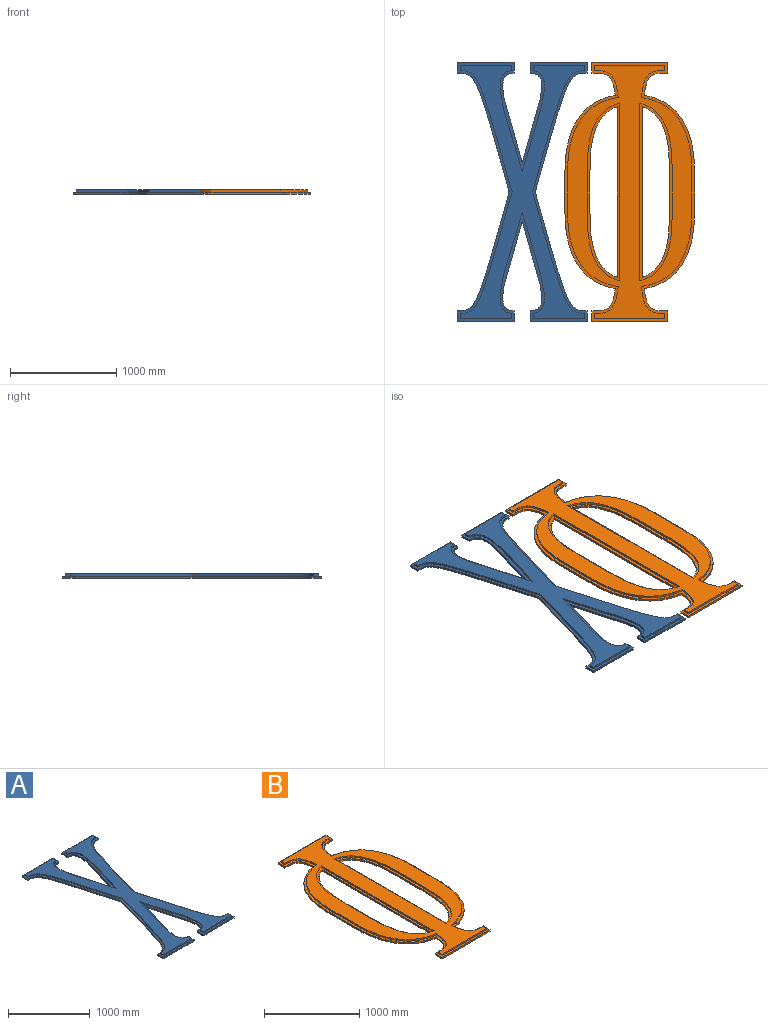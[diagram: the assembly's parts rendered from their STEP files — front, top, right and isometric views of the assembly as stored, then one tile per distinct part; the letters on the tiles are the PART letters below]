
ASSEMBLY  parts=2 mates=2
PART A: 55 faces, bbox 1219.2x2438.4x38.1 mm
  f0: plane 2438.4x1219.2mm, normal (0,0,1), area 313882.5mm2, adj f1,f2,f4,f5,f6,f7,f8,f9
  f1: plane 533.4x19.05mm, normal (0,1,0), area 10161.3mm2, adj f0,f2,f3,f6
  f2: plane 101.6x19.05mm, normal (-1,0,0), area 1935.5mm2, adj f0,f1,f3,f7
  f3: plane 2438.4x1219.2mm, normal (0,0,-1), area 1136315.4mm2, adj f1,f2,f4,f5,f6,f7,f16,f17
  f4: plane 613.66x172.59mm, normal (0.96,0.27,0), area 12143.9mm2, adj f0,f3,f5,f18
  f5: extruded ~224.54x106.77mm, area 5550.7mm2, adj f0,f3,f4,f6
  f6: plane 101.6x19.05mm, normal (1,0,0), area 1935.5mm2, adj f0,f1,f3,f5
  f7: extruded ~1117.6x487.68mm, area 24421.9mm2, adj f0,f2,f3,f34
  f8: plane 50.95x19.05mm, normal (-1,0,0), area 970.5mm2, adj f0,f9,f14,f15
  f9: extruded ~1117.45x481.52mm, area 24198.9mm2, adj f0,f8,f10,f15
  f10: plane 25.4x19.05mm, normal (-0.96,-0.27,0), area 502.7mm2, adj f0,f9,f15,f37
  f11: plane 81.62x25.4mm, normal (0.95,0.3,0), area 1628.3mm2, adj f0,f12,f15,f25
  f12: extruded ~866.26x183mm, area 18053.1mm2, adj f0,f11,f13,f15
  f13: plane 52.15x19.05mm, normal (1,0,0), area 993.5mm2, adj f0,f12,f14,f15
  f14: plane 482.6x19.05mm, normal (0,1,0), area 9193.5mm2, adj f0,f8,f13,f15
  f15: plane 2387.6x1172.43mm, normal (0,0,1), area 822432.8mm2, adj f8,f9,f10,f11,f12,f13,f14,f22
  f16: plane 533.4x19.05mm, normal (0,1,0), area 10161.3mm2, adj f0,f3,f17,f20
  f17: plane 101.6x19.05mm, normal (1,0,0), area 1935.5mm2, adj f0,f3,f16,f21
  f18: plane 613.66x172.59mm, normal (-0.96,0.27,0), area 12143.9mm2, adj f0,f3,f4,f19
  f19: extruded ~224.54x106.77mm, area 5550.7mm2, adj f0,f3,f18,f20
  f20: plane 101.6x19.05mm, normal (-1,0,0), area 1935.5mm2, adj f0,f3,f16,f19
  f21: extruded ~1117.6x487.68mm, area 24421.9mm2, adj f0,f3,f17,f47
  f22: plane 50.95x19.05mm, normal (1,0,0), area 970.5mm2, adj f0,f15,f23,f28
  f23: extruded ~1117.45x481.52mm, area 24198.9mm2, adj f0,f15,f22,f24
  f24: plane 25.4x19.05mm, normal (0.96,-0.27,0), area 502.7mm2, adj f0,f15,f23,f50
  f25: plane 81.62x25.4mm, normal (-0.95,0.3,0), area 1628.3mm2, adj f0,f11,f15,f26
  f26: extruded ~866.26x183mm, area 18053.1mm2, adj f0,f15,f25,f27
  f27: plane 52.15x19.05mm, normal (-1,0,0), area 993.5mm2, adj f0,f15,f26,f28
  f28: plane 482.6x19.05mm, normal (0,1,0), area 9193.5mm2, adj f0,f15,f22,f27
  f29: plane 533.4x19.05mm, normal (0,-1,0), area 10161.3mm2, adj f0,f3,f30,f33
  f30: plane 101.6x19.05mm, normal (-1,0,0), area 1935.5mm2, adj f0,f3,f29,f34
  f31: plane 613.66x172.59mm, normal (0.96,-0.27,0), area 12143.9mm2, adj f0,f3,f32,f44
  f32: extruded ~224.54x106.77mm, area 5550.7mm2, adj f0,f3,f31,f33
  f33: plane 101.6x19.05mm, normal (1,0,0), area 1935.5mm2, adj f0,f3,f29,f32
  f34: extruded ~1117.6x487.68mm, area 24421.9mm2, adj f0,f3,f7,f30
  f35: plane 50.95x19.05mm, normal (-1,0,0), area 970.5mm2, adj f0,f15,f36,f41
  f36: extruded ~1117.45x481.52mm, area 24198.9mm2, adj f0,f15,f35,f37
  f37: plane 25.4x19.05mm, normal (-0.96,0.27,0), area 502.7mm2, adj f0,f10,f15,f36
  f38: plane 81.62x25.4mm, normal (0.95,-0.3,0), area 1628.3mm2, adj f0,f15,f39,f51
  f39: extruded ~866.26x183mm, area 18053.1mm2, adj f0,f15,f38,f40
  f40: plane 52.15x19.05mm, normal (1,0,0), area 993.5mm2, adj f0,f15,f39,f41
  f41: plane 482.6x19.05mm, normal (0,-1,0), area 9193.5mm2, adj f0,f15,f35,f40
  f42: plane 533.4x19.05mm, normal (0,-1,0), area 10161.3mm2, adj f0,f3,f43,f46
  f43: plane 101.6x19.05mm, normal (1,0,0), area 1935.5mm2, adj f0,f3,f42,f47
  f44: plane 613.66x172.59mm, normal (-0.96,-0.27,0), area 12143.9mm2, adj f0,f3,f31,f45
  f45: extruded ~224.54x106.77mm, area 5550.7mm2, adj f0,f3,f44,f46
  f46: plane 101.6x19.05mm, normal (-1,0,0), area 1935.5mm2, adj f0,f3,f42,f45
  f47: extruded ~1117.6x487.68mm, area 24421.9mm2, adj f0,f3,f21,f43
  f48: plane 50.95x19.05mm, normal (1,0,0), area 970.5mm2, adj f0,f15,f49,f54
  f49: extruded ~1117.45x481.52mm, area 24198.9mm2, adj f0,f15,f48,f50
  f50: plane 25.4x19.05mm, normal (0.96,0.27,0), area 502.7mm2, adj f0,f15,f24,f49
  f51: plane 81.62x25.4mm, normal (-0.95,-0.3,0), area 1628.3mm2, adj f0,f15,f38,f52
  f52: extruded ~866.26x183mm, area 18053.1mm2, adj f0,f15,f51,f53
  f53: plane 52.15x19.05mm, normal (-1,0,0), area 993.5mm2, adj f0,f15,f52,f54
  f54: plane 482.6x19.05mm, normal (0,-1,0), area 9193.5mm2, adj f0,f15,f48,f53
PART B: 53 faces, bbox 1219.2x2438.4x38.1 mm
  f0: plane 1670.71x319.18mm, normal (0,0,1), area 89086.3mm2, adj f8,f9,f10,f16,f17,f18,f39,f44
  f1: plane 2438.4x1219.2mm, normal (0,0,1), area 195561.9mm2, adj f2,f3,f5,f6,f7,f11,f12,f13
  f2: plane 711.2x19.05mm, normal (0,1,0), area 13548.4mm2, adj f1,f4,f6,f23
  f3: plane 381x19.05mm, normal (-1,0,0), area 7258.1mm2, adj f1,f4,f5,f36
  f4: plane 2438.4x1219.2mm, normal (0,0,-1), area 1517111.4mm2, adj f2,f3,f5,f6,f7,f8,f9,f10
  f5: extruded ~719.03x473.41mm, area 18049.5mm2, adj f1,f3,f4,f7
  f6: plane 101.6x19.05mm, normal (-1,0,0), area 1935.5mm2, adj f1,f2,f4,f7
  f7: extruded ~219.41x208.07mm, area 6774.8mm2, adj f1,f4,f5,f6
  f8: plane 381x19.05mm, normal (1,0,0), area 7258.1mm2, adj f0,f4,f9,f39
  f9: extruded ~611.51x257.18mm, area 13546.1mm2, adj f0,f4,f8,f10
  f10: plane 1604.02x19.05mm, normal (-1,0,0), area 30556.7mm2, adj f0,f4,f9,f39
  f11: plane 660.4x19.05mm, normal (0,1,0), area 12580.6mm2, adj f1,f12,f19,f28
  f12: plane 50.85x19.05mm, normal (-1,0,0), area 968.7mm2, adj f1,f11,f13,f19
  f13: extruded ~254.76x221.91mm, area 7460.1mm2, adj f1,f12,f14,f19
  f14: extruded ~697.69x475.91mm, area 17826.8mm2, adj f1,f13,f15,f19
  f15: plane 381x19.05mm, normal (-1,0,0), area 7258mm2, adj f1,f14,f19,f43
  f16: plane 381x19.05mm, normal (1,0,0), area 7258mm2, adj f0,f17,f19,f44
  f17: extruded ~644.61x307.98mm, area 14810.3mm2, adj f0,f16,f18,f19
  f18: plane 1670.21x19.05mm, normal (-1,0,0), area 31817.6mm2, adj f0,f17,f19,f44
  f19: plane 2387.6x1168.4mm, normal (0,0,1), area 1143377mm2, adj f11,f12,f13,f14,f15,f16,f17,f18
  f20: plane 1670.71x319.18mm, normal (0,0,1), area 89086.3mm2, adj f25,f26,f27,f32,f33,f34,f48,f52
  f21: plane 381x19.05mm, normal (1,0,0), area 7258.1mm2, adj f1,f4,f22,f45
  f22: extruded ~719.03x473.41mm, area 18049.5mm2, adj f1,f4,f21,f24
  f23: plane 101.6x19.05mm, normal (1,0,0), area 1935.5mm2, adj f1,f2,f4,f24
  f24: extruded ~219.41x208.07mm, area 6774.8mm2, adj f1,f4,f22,f23
  f25: plane 381x19.05mm, normal (-1,0,0), area 7258.1mm2, adj f4,f20,f26,f48
  f26: extruded ~611.51x257.18mm, area 13546.1mm2, adj f4,f20,f25,f27
  f27: plane 1604.02x19.05mm, normal (1,0,0), area 30556.7mm2, adj f4,f20,f26,f48
  f28: plane 50.85x19.05mm, normal (1,0,0), area 968.7mm2, adj f1,f11,f19,f29
  f29: extruded ~254.76x221.91mm, area 7460.1mm2, adj f1,f19,f28,f30
  f30: extruded ~697.69x475.91mm, area 17826.8mm2, adj f1,f19,f29,f31
  f31: plane 381x19.05mm, normal (1,0,0), area 7258mm2, adj f1,f19,f30,f51
  f32: plane 381x19.05mm, normal (-1,0,0), area 7258mm2, adj f19,f20,f33,f52
  f33: extruded ~644.61x307.98mm, area 14810.3mm2, adj f19,f20,f32,f34
  f34: plane 1670.21x19.05mm, normal (1,0,0), area 31817.6mm2, adj f19,f20,f33,f52
  f35: plane 711.2x19.05mm, normal (0,-1,0), area 13548.4mm2, adj f1,f4,f37,f46
  f36: extruded ~719.03x473.41mm, area 18049.5mm2, adj f1,f3,f4,f38
  f37: plane 101.6x19.05mm, normal (-1,0,0), area 1935.5mm2, adj f1,f4,f35,f38
  f38: extruded ~219.41x208.07mm, area 6774.8mm2, adj f1,f4,f36,f37
  f39: extruded ~611.51x257.18mm, area 13546.1mm2, adj f0,f4,f8,f10
  f40: plane 660.4x19.05mm, normal (0,-1,0), area 12580.6mm2, adj f1,f19,f41,f49
  f41: plane 50.85x19.05mm, normal (-1,0,0), area 968.7mm2, adj f1,f19,f40,f42
  f42: extruded ~254.76x221.91mm, area 7460.1mm2, adj f1,f19,f41,f43
  f43: extruded ~697.69x475.91mm, area 17826.8mm2, adj f1,f15,f19,f42
  f44: extruded ~644.61x307.98mm, area 14810.3mm2, adj f0,f16,f18,f19
  f45: extruded ~719.03x473.41mm, area 18049.5mm2, adj f1,f4,f21,f47
  f46: plane 101.6x19.05mm, normal (1,0,0), area 1935.5mm2, adj f1,f4,f35,f47
  f47: extruded ~219.41x208.07mm, area 6774.8mm2, adj f1,f4,f45,f46
  f48: extruded ~611.51x257.18mm, area 13546.1mm2, adj f4,f20,f25,f27
  f49: plane 50.85x19.05mm, normal (1,0,0), area 968.7mm2, adj f1,f19,f40,f50
  f50: extruded ~254.76x221.91mm, area 7460.1mm2, adj f1,f19,f49,f51
  f51: extruded ~697.69x475.91mm, area 17826.8mm2, adj f1,f19,f31,f50
  f52: extruded ~644.61x307.98mm, area 14810.3mm2, adj f19,f20,f32,f34
PLACE A t=(-304.87,-4.29,-84.25)mm
PLACE B t=(706.44,-4.29,-84.25)mm
MATE planar B.f2 <-> A.f1  axis (0,1,0) through (706.44,1214.91,-74.73)mm
MATE planar A.f0 <-> B.f0  axis (0,0,1) through (-304.89,-4.33,-65.2)mm
